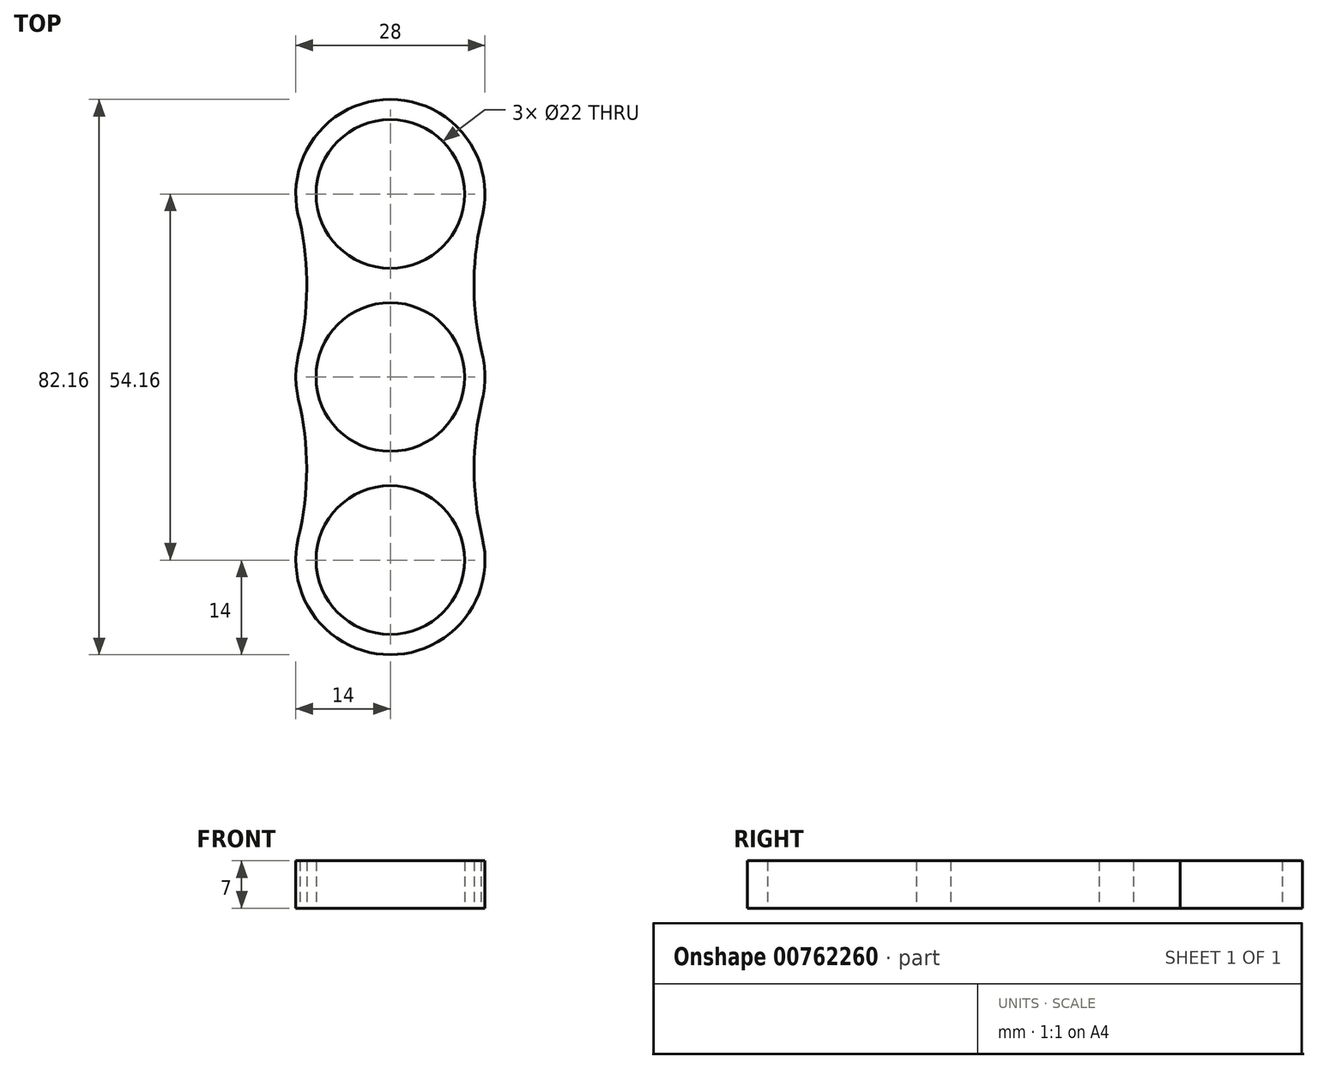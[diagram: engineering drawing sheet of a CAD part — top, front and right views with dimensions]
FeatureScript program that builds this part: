
annotation { "Feature Type Name" : "Feature", "Feature Type Description" : "" }
export const myFeature = defineFeature(function(context is Context, id is Id, definition is map)
    precondition{}
    {
        {
            var Q0;
            Q0=qCreatedBy(makeId("Top.planeOp"),FACE);
            var sketch = newSketch(context, id + "F0", { "sketchPlane" : qUnion([Q0])});
            skCircle(sketch, "E0", {"center": v(0, 0) * mm, "radius": 11 * mm});
            skCircle(sketch, "E1", {"center": v(0, 27.08) * mm, "radius": 11 * mm});
            skCircle(sketch, "E2", {"center": v(0, -27.08) * mm, "radius": 11 * mm});
            skSolve(sketch);
        }
        {
            var Q0;
            Q0=qCreatedBy(makeId("Top.planeOp"),FACE);
            var sketch = newSketch(context, id + "F1", { "sketchPlane" : qUnion([Q0])});
            skPoint(sketch, "E3.0", {"position": v(0, 27.08) * mm});
            skPoint(sketch, "E4.0", {"position": v(0, -27.08) * mm});
            skPoint(sketch, "E5.0", {"position": v(0, 0) * mm});
            skCircle(sketch, "E6", {"center": v(0, 27.08) * mm, "radius": 14 * mm});
            skCircle(sketch, "E7", {"center": v(0, -27.08) * mm, "radius": 14 * mm});
            skArc(sketch, "E8", {"start": v(-13.61, 3.27) * mm, "mid": v(-12.38, 13.13) * mm, "end": v(-13.4, 23.01) * mm});
            skArc(sketch, "E9", {"start": v(-13.61, -23.81) * mm, "mid": v(-12.4, -13.54) * mm, "end": v(-13.61, -3.27) * mm});
            skCircle(sketch, "E10", {"center": v(0, 0) * mm, "radius": 14 * mm});
            skArc(sketch, "E11.MirrorCS", {"start": v(13.61, 3.27) * mm, "mid": v(12.38, 13.13) * mm, "end": v(13.4, 23.01) * mm});
            skArc(sketch, "E12.MirrorCS", {"start": v(13.61, -23.81) * mm, "mid": v(12.4, -13.54) * mm, "end": v(13.61, -3.27) * mm});
            skCircle(sketch, "E13.0", {"center": v(0, 27.08) * mm, "radius": 11 * mm});
            skCircle(sketch, "E14.0", {"center": v(0, 0) * mm, "radius": 11 * mm});
            skCircle(sketch, "E15.0", {"center": v(0, -27.08) * mm, "radius": 11 * mm});
            skSolve(sketch);
        }
        {
            var Q0;
            Q0 = qSketchRegion(id + "F1", true);
            var Q1;
            {var subQ0=sQuery(id+"F1.wireOp",EDGE,"E10");var subQ1=sQuery(id+"F1.wireOp",EDGE,"E7");var subQ2=makeQuery(id+"F1.imprint","INTERSECT",VERTEX,{"disambiguationData":[OD(0.0)],"derivedFrom":[subQ1,subQ0]});Q1=makeQuery(id+"F1.imprint","IMPRINT",FACE,{"disambiguationData":[TD([[makeQuery(id+"F1.imprint","IMPRINT",EDGE,{"disambiguationData":[TD([[subQ2,-1.0]])],"derivedFrom":subQ1}),1.0]])]});}
            var Q2;
            {var subQ0=sQuery(id+"F1.wireOp",EDGE,"E10");var subQ1=sQuery(id+"F1.wireOp",EDGE,"E6");var subQ2=makeQuery(id+"F1.imprint","INTERSECT",VERTEX,{"disambiguationData":[OD(0.0)],"derivedFrom":[subQ1,subQ0]});Q2=makeQuery(id+"F1.imprint","IMPRINT",FACE,{"disambiguationData":[TD([[makeQuery(id+"F1.imprint","IMPRINT",EDGE,{"disambiguationData":[TD([[subQ2,-1.0]])],"derivedFrom":subQ1}),1.0]])]});}
            extrude(context, id + "F2", {"entities" : qUnion([Q0, Q1, Q2]), "depth" : 7 * mm, "offsetDistance" : 25.4 * mm});
        }
    });
